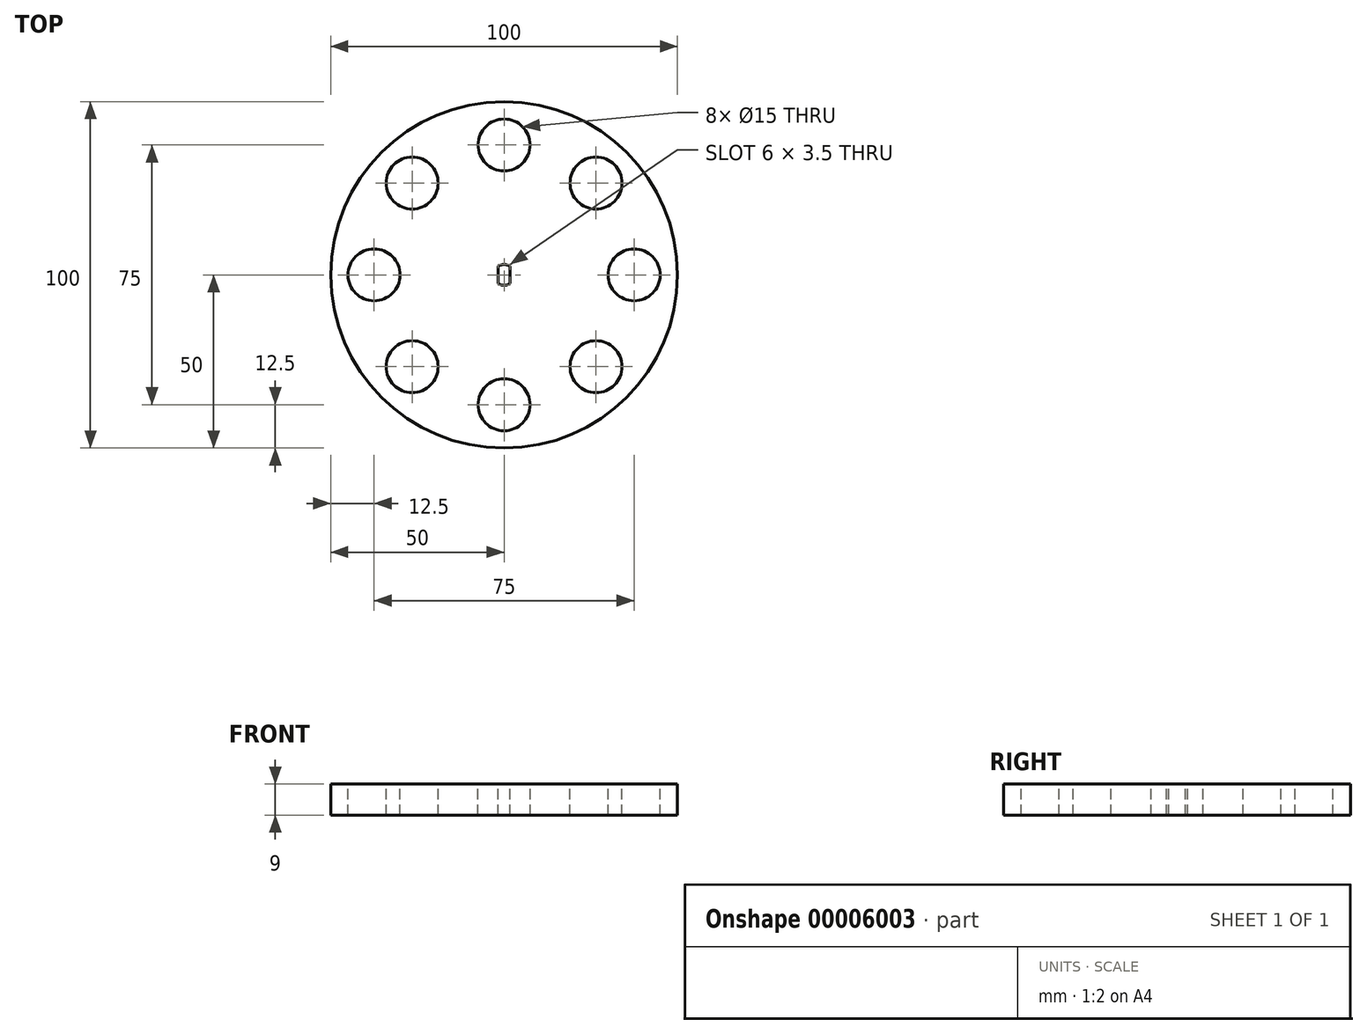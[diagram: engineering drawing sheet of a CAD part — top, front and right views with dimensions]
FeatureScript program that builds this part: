
annotation { "Feature Type Name" : "Feature", "Feature Type Description" : "" }
export const myFeature = defineFeature(function(context is Context, id is Id, definition is map)
    precondition{}
    {
        {
            var Q0;
            Q0=qCreatedBy(makeId("Top.planeOp"),FACE);
            var sketch = newSketch(context, id + "F0", { "sketchPlane" : qUnion([Q0])});
            skCircle(sketch, "E0", {"center": v(0, 0) * mm, "radius": 50 * mm});
            skSolve(sketch);
        }
        {
            var Q0;
            Q0 = qSketchRegion(id + "F0", true);
            extrude(context, id + "F1", {"entities" : qUnion([Q0]), "depth" : 9 * mm});
        }
        {
            var Q0;
            Q0=makeQuery(id+"F1.opExtrude","CAP_FACE",FACE,{"disambiguationData":[OSD([sQuery(id+"F0.wireOp",EDGE,"E0")])],"isStart":false});
            var sketch = newSketch(context, id + "F2", { "sketchPlane" : qUnion([Q0])});
            skCircle(sketch, "E1", {"center": v(37.5, 0) * mm, "radius": 7.5 * mm});
            skCircle(sketch, "E2.1.0", {"center": v(26.52, 26.52) * mm, "radius": 7.5 * mm});
            skCircle(sketch, "E2.2.0", {"center": v(0, 37.5) * mm, "radius": 7.5 * mm});
            skCircle(sketch, "E2.3.0", {"center": v(-26.52, 26.52) * mm, "radius": 7.5 * mm});
            skCircle(sketch, "E2.4.0", {"center": v(-37.5, 0) * mm, "radius": 7.5 * mm});
            skCircle(sketch, "E2.5.0", {"center": v(-26.52, -26.52) * mm, "radius": 7.5 * mm});
            skPoint(sketch, "E2.center", {"position": v(0, 0) * mm});
            skCircle(sketch, "E3.1.6.0", {"center": v(0, -37.5) * mm, "radius": 7.5 * mm});
            skCircle(sketch, "E3.1.7.0", {"center": v(26.52, -26.52) * mm, "radius": 7.5 * mm});
            skSolve(sketch);
        }
        {
            var Q0;
            Q0 = qSketchRegion(id + "F2", true);
            extrude(context, id + "F3", {"entities" : qUnion([Q0]), "operationType" : NewBodyOperationType.REMOVE, "endBound" : BoundingType.THROUGH_ALL, "oppositeDirection" : true, "depth" : 25 * mm});
        }
        {
            var Q0;
            Q0=makeQuery(id+"F1.opExtrude","CAP_FACE",FACE,{"disambiguationData":[OSD([sQuery(id+"F0.wireOp",EDGE,"E0")])],"isStart":false});
            var sketch = newSketch(context, id + "F4", { "sketchPlane" : qUnion([Q0])});
            skArc(sketch, "E4", {"start": v(-1.75, -2.44) * mm, "mid": v(0, -3) * mm, "end": v(1.75, -2.44) * mm});
            skLineSegment(sketch, "E5.rect.left", {"start": v(1.75, 2.44) * mm, "end": v(1.75, -2.44) * mm});
            skLineSegment(sketch, "E5.rect.right", {"start": v(-1.75, 2.44) * mm, "end": v(-1.75, -2.44) * mm});
            skArc(sketch, "E6.trimOffspring", {"start": v(1.75, 2.44) * mm, "mid": v(0, 3) * mm, "end": v(-1.75, 2.44) * mm});
            skSolve(sketch);
        }
        {
            var Q0;
            Q0=makeQuery(id+"F4.imprint","IMPRINT",FACE,{"disambiguationData":[TD([[makeQuery(id+"F4.imprint","IMPRINT",EDGE,{"derivedFrom":sQuery(id+"F4.wireOp",EDGE,"E4")}),-1.0]])]});
            extrude(context, id + "F5", {"entities" : qUnion([Q0]), "operationType" : NewBodyOperationType.INTERSECT, "endBound" : BoundingType.THROUGH_ALL, "oppositeDirection" : true, "depth" : 25 * mm});
        }
    });
